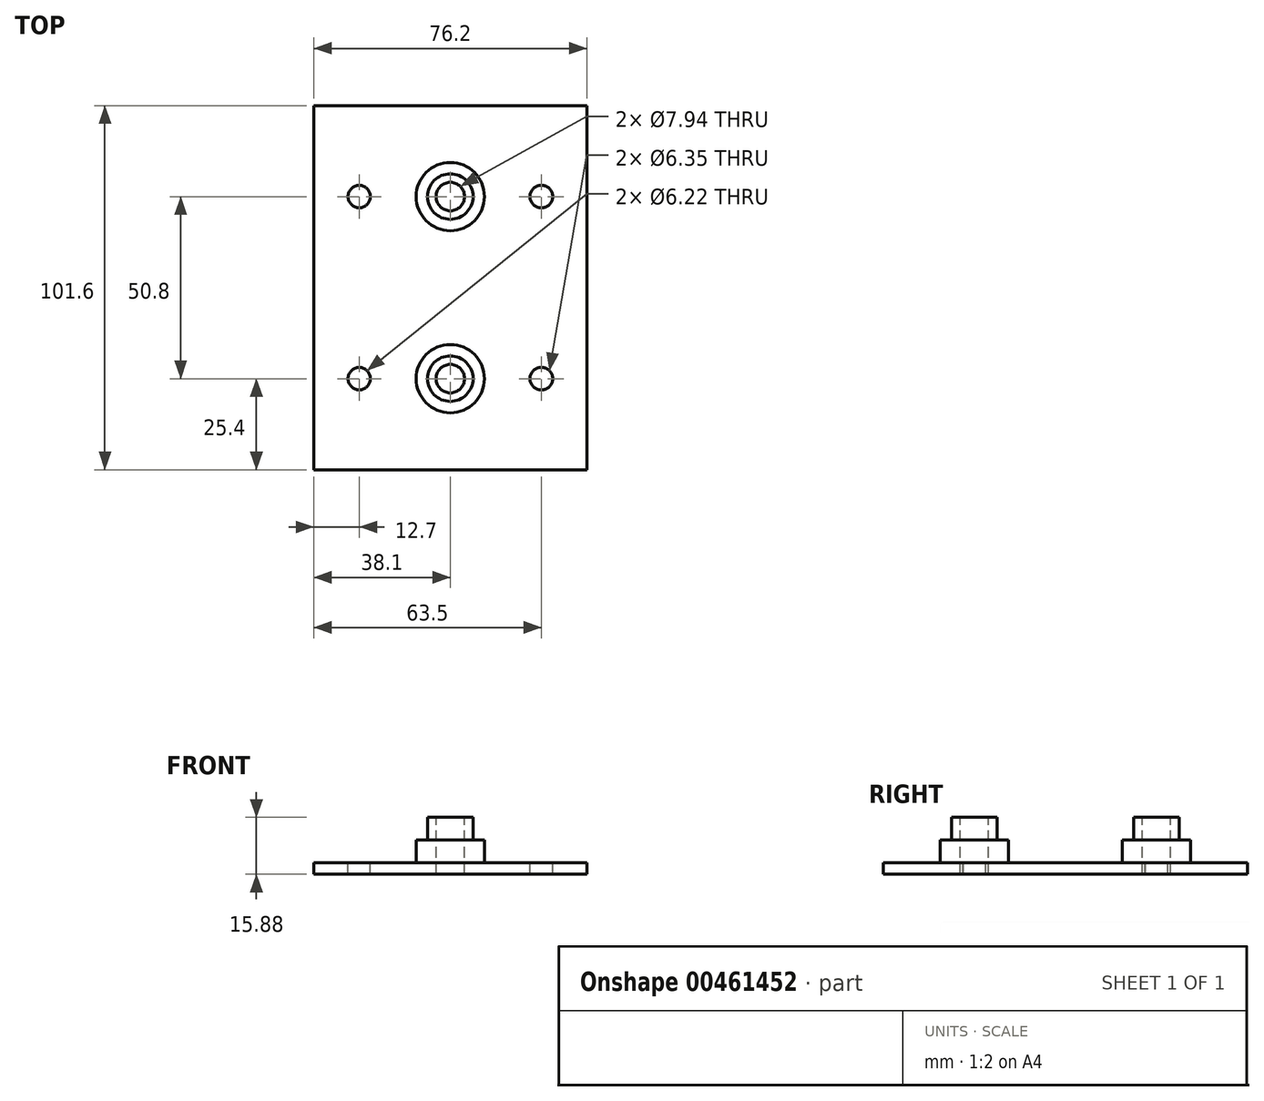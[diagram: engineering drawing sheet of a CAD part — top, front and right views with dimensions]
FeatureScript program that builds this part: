
annotation { "Feature Type Name" : "Feature", "Feature Type Description" : "" }
export const myFeature = defineFeature(function(context is Context, id is Id, definition is map)
    precondition{}
    {
        {
            var Q0;
            Q0=qCreatedBy(makeId("Top.planeOp"),FACE);
            var sketch = newSketch(context, id + "F0", { "sketchPlane" : qUnion([Q0])});
            skLineSegment(sketch, "E0.bottom", {"start": v(-38.1, 50.8) * mm, "end": v(38.1, 50.8) * mm});
            skLineSegment(sketch, "E0.top", {"start": v(-38.1, -50.8) * mm, "end": v(38.1, -50.8) * mm});
            skLineSegment(sketch, "E0.left", {"start": v(-38.1, 50.8) * mm, "end": v(-38.1, -50.8) * mm});
            skLineSegment(sketch, "E0.right", {"start": v(38.1, 50.8) * mm, "end": v(38.1, -50.8) * mm});
            skPoint(sketch, "E0.middle", {"position": v(0, 0) * mm});
            skSolve(sketch);
        }
        {
            var Q0;
            Q0=makeQuery(id+"F0.imprint","IMPRINT",FACE,{"disambiguationData":[TD([[makeQuery(id+"F0.imprint","IMPRINT",EDGE,{"derivedFrom":sQuery(id+"F0.wireOp",EDGE,"E0.bottom")}),-1.0]])]});
            extrude(context, id + "F1", {"entities" : qUnion([Q0]), "depth" : 3.17 * mm, "offsetDistance" : 25.4 * mm});
        }
        {
            var Q0;
            Q0=makeQuery(id+"F1.opExtrude","CAP_FACE",FACE,{"disambiguationData":[OSD([sQuery(id+"F0.wireOp",EDGE,"E0.bottom"),sQuery(id+"F0.wireOp",EDGE,"E0.top"),sQuery(id+"F0.wireOp",EDGE,"E0.left"),sQuery(id+"F0.wireOp",EDGE,"E0.right")])],"isStart":false});
            var sketch = newSketch(context, id + "F2", { "sketchPlane" : qUnion([Q0])});
            skCircle(sketch, "E1", {"center": v(0, 25.4) * mm, "radius": 6.35 * mm});
            skCircle(sketch, "E2", {"center": v(0, -25.4) * mm, "radius": 6.35 * mm});
            skSolve(sketch);
        }
        {
            var Q0;
            Q0=makeQuery(id+"F2.imprint","IMPRINT",FACE,{"disambiguationData":[TD([[makeQuery(id+"F2.imprint","IMPRINT",EDGE,{"derivedFrom":sQuery(id+"F2.wireOp",EDGE,"E1")}),1.0]])]});
            var Q1;
            Q1=makeQuery(id+"F2.imprint","IMPRINT",FACE,{"disambiguationData":[TD([[makeQuery(id+"F2.imprint","IMPRINT",EDGE,{"derivedFrom":sQuery(id+"F2.wireOp",EDGE,"E2")}),1.0]])]});
            extrude(context, id + "F3", {"entities" : qUnion([Q0, Q1]), "operationType" : NewBodyOperationType.ADD, "depth" : 12.7 * mm, "offsetDistance" : 25.4 * mm});
        }
        {
            var Q0;
            Q0=makeQuery(id+"F3.opExtrude","CAP_FACE",FACE,{"disambiguationData":[OSD([sQuery(id+"F2.wireOp",EDGE,"E1")])],"isStart":false});
            var sketch = newSketch(context, id + "F4", { "sketchPlane" : qUnion([Q0])});
            skCircle(sketch, "E3", {"center": v(0, 25.4) * mm, "radius": 3.97 * mm});
            skSolve(sketch);
        }
        {
            var Q0;
            Q0=makeQuery(id+"F3.opExtrude","CAP_FACE",FACE,{"disambiguationData":[OSD([sQuery(id+"F2.wireOp",EDGE,"E2")])],"isStart":false});
            var sketch = newSketch(context, id + "F5", { "sketchPlane" : qUnion([Q0])});
            skCircle(sketch, "E4", {"center": v(0, -25.4) * mm, "radius": 3.97 * mm});
            skSolve(sketch);
        }
        {
            var Q0;
            Q0=makeQuery(id+"F4.imprint","IMPRINT",FACE,{"disambiguationData":[TD([[makeQuery(id+"F4.imprint","IMPRINT",EDGE,{"derivedFrom":sQuery(id+"F4.wireOp",EDGE,"E3")}),1.0]])]});
            var Q1;
            Q1=makeQuery(id+"F5.imprint","IMPRINT",FACE,{"disambiguationData":[TD([[makeQuery(id+"F5.imprint","IMPRINT",EDGE,{"derivedFrom":sQuery(id+"F5.wireOp",EDGE,"E4")}),1.0]])]});
            extrude(context, id + "F6", {"entities" : qUnion([Q0, Q1]), "operationType" : NewBodyOperationType.REMOVE, "oppositeDirection" : true, "depth" : 38.1 * mm, "offsetDistance" : 25.4 * mm});
        }
        {
            var Q0;
            Q0=makeQuery(id+"F1.opExtrude","CAP_FACE",FACE,{"disambiguationData":[OSD([sQuery(id+"F0.wireOp",EDGE,"E0.bottom"),sQuery(id+"F0.wireOp",EDGE,"E0.top"),sQuery(id+"F0.wireOp",EDGE,"E0.left"),sQuery(id+"F0.wireOp",EDGE,"E0.right")])],"isStart":false});
            var sketch = newSketch(context, id + "F7", { "sketchPlane" : qUnion([Q0])});
            skCircle(sketch, "E5", {"center": v(25.4, 25.4) * mm, "radius": 3.18 * mm});
            skCircle(sketch, "E6", {"center": v(25.4, -25.4) * mm, "radius": 3.18 * mm});
            skCircle(sketch, "E7", {"center": v(-25.4, 25.4) * mm, "radius": 3.11 * mm});
            skCircle(sketch, "E8", {"center": v(-25.4, -25.4) * mm, "radius": 3.11 * mm});
            skSolve(sketch);
        }
        {
            var Q0;
            Q0=makeQuery(id+"F7.imprint","IMPRINT",FACE,{"disambiguationData":[TD([[makeQuery(id+"F7.imprint","IMPRINT",EDGE,{"derivedFrom":sQuery(id+"F7.wireOp",EDGE,"E5")}),1.0]])]});
            var Q1;
            Q1=makeQuery(id+"F7.imprint","IMPRINT",FACE,{"disambiguationData":[TD([[makeQuery(id+"F7.imprint","IMPRINT",EDGE,{"derivedFrom":sQuery(id+"F7.wireOp",EDGE,"E6")}),1.0]])]});
            var Q2;
            Q2=makeQuery(id+"F7.imprint","IMPRINT",FACE,{"disambiguationData":[TD([[makeQuery(id+"F7.imprint","IMPRINT",EDGE,{"derivedFrom":sQuery(id+"F7.wireOp",EDGE,"E7")}),1.0]])]});
            var Q3;
            Q3=makeQuery(id+"F7.imprint","IMPRINT",FACE,{"disambiguationData":[TD([[makeQuery(id+"F7.imprint","IMPRINT",EDGE,{"derivedFrom":sQuery(id+"F7.wireOp",EDGE,"E8")}),1.0]])]});
            extrude(context, id + "F8", {"entities" : qUnion([Q0, Q1, Q2, Q3]), "operationType" : NewBodyOperationType.REMOVE, "oppositeDirection" : true, "depth" : 25.4 * mm, "offsetDistance" : 25.4 * mm});
        }
        {
            var Q0;
            Q0=makeQuery(id+"F1.opExtrude","CAP_FACE",FACE,{"disambiguationData":[OSD([sQuery(id+"F0.wireOp",EDGE,"E0.bottom"),sQuery(id+"F0.wireOp",EDGE,"E0.top"),sQuery(id+"F0.wireOp",EDGE,"E0.left"),sQuery(id+"F0.wireOp",EDGE,"E0.right")])],"isStart":false});
            var sketch = newSketch(context, id + "F9", { "sketchPlane" : qUnion([Q0])});
            skCircle(sketch, "E9", {"center": v(0, 25.4) * mm, "radius": 9.53 * mm});
            skCircle(sketch, "E10", {"center": v(0, -25.4) * mm, "radius": 9.53 * mm});
            skSolve(sketch);
        }
        {
            var Q0;
            Q0=makeQuery(id+"F9.imprint","IMPRINT",FACE,{"disambiguationData":[TD([[makeQuery(id+"F9.imprint","IMPRINT",EDGE,{"derivedFrom":sQuery(id+"F9.wireOp",EDGE,"E9")}),1.0]])]});
            var Q1;
            Q1=makeQuery(id+"F9.imprint","IMPRINT",FACE,{"disambiguationData":[TD([[makeQuery(id+"F9.imprint","IMPRINT",EDGE,{"derivedFrom":sQuery(id+"F9.wireOp",EDGE,"E10")}),1.0]])]});
            extrude(context, id + "F10", {"entities" : qUnion([Q0, Q1]), "operationType" : NewBodyOperationType.ADD, "depth" : 6.35 * mm, "offsetDistance" : 25.4 * mm});
        }
    });
